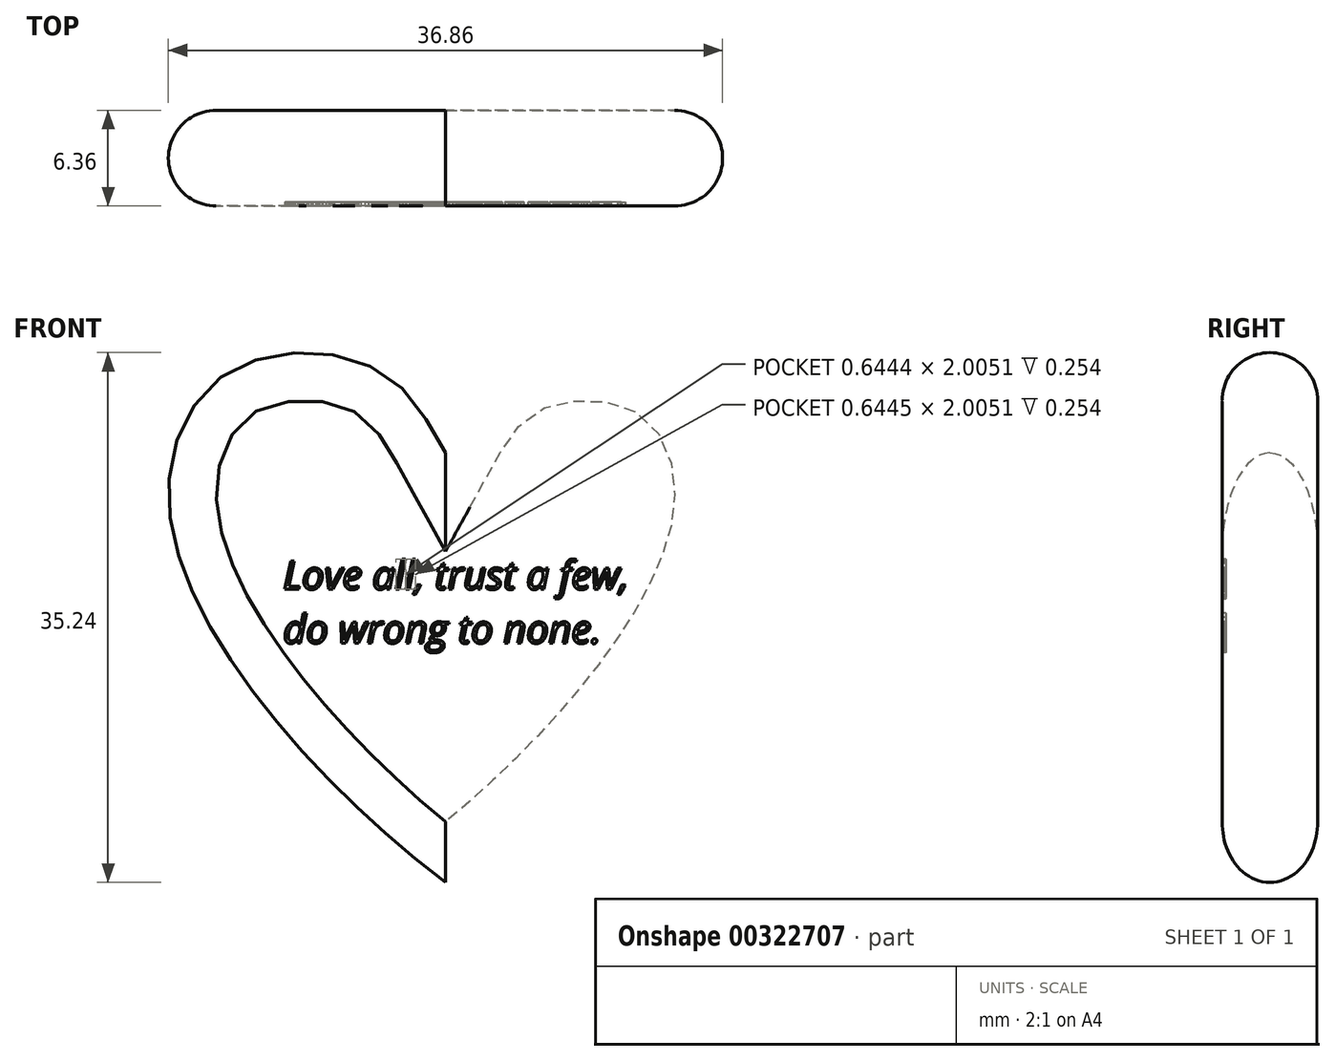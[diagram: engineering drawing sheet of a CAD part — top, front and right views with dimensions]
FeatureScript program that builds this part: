
annotation { "Feature Type Name" : "Feature", "Feature Type Description" : "" }
export const myFeature = defineFeature(function(context is Context, id is Id, definition is map)
    precondition{}
    {
        {
            var Q0;
            Q0=qCreatedBy(makeId("Front.planeOp"),FACE);
            var sketch = newSketch(context, id + "F0", { "sketchPlane" : qUnion([Q0])});
            skLineSegment(sketch, "E0", {"start": v(0, -28.57) * mm, "end": v(0, 0) * mm});
            skFitSpline(sketch, "E1", {"points": [v(0, 0) * mm, v(-4.62, 5.57) * mm, v(-14.08, 5.57) * mm, v(-18.41, -2.03) * mm, v(-14.08, -14.1) * mm, v(0, -28.58) * mm], "startDerivative": vector(-22.34, 40.38) * mm, "endDerivative": vector(58.02, -43.63) * mm});
            skFitSpline(sketch, "E2.MirrorCS", {"points": [v(0, 0) * mm, v(4.62, 5.57) * mm, v(14.08, 5.57) * mm, v(18.41, -2.03) * mm, v(14.08, -14.1) * mm, v(0, -28.58) * mm], "startDerivative": vector(22.34, 40.38) * mm, "endDerivative": vector(-58.02, -43.63) * mm});
            skSolve(sketch);
        }
        {
            var Q0;
            Q0=makeQuery(id+"F0.imprint","IMPRINT",FACE,{"disambiguationData":[TD([[makeQuery(id+"F0.imprint","IMPRINT",EDGE,{"derivedFrom":sQuery(id+"F0.wireOp",EDGE,"E0")}),1.0]])]});
            var Q1;
            Q1=makeQuery(id+"F0.imprint","IMPRINT",FACE,{"disambiguationData":[TD([[makeQuery(id+"F0.imprint","IMPRINT",EDGE,{"derivedFrom":sQuery(id+"F0.wireOp",EDGE,"E0")}),-1.0]])]});
            extrude(context, id + "F1", {"entities" : qUnion([Q0, Q1]), "endBound" : BoundingType.SYMMETRIC, "depth" : 6.35 * mm});
        }
        {
            var Q0;
            Q0=makeQuery(id+"F1.opExtrude","CAP_FACE",FACE,{"disambiguationData":[OSD([sQuery(id+"F0.wireOp",EDGE,"E1"),sQuery(id+"F0.wireOp",EDGE,"E2.MirrorCS")])],"isStart":false});
            var Q1;
            Q1=makeQuery(id+"F1.opExtrude","CAP_FACE",FACE,{"disambiguationData":[OSD([sQuery(id+"F0.wireOp",EDGE,"E1"),sQuery(id+"F0.wireOp",EDGE,"E2.MirrorCS")])],"isStart":true});
            fillet(context, id + "F2", {"entities" : qUnion([Q0, Q1]), "radius" : 3.17 * mm, "tangentPropagation" : true, "allowEdgeOverflow" : false});
        }
        {
            var Q0;
            Q0=makeQuery(id+"F1.opExtrude","CAP_FACE",FACE,{"disambiguationData":[OSD([sQuery(id+"F0.wireOp",EDGE,"E1"),sQuery(id+"F0.wireOp",EDGE,"E2.MirrorCS")])],"isStart":false});
            var sketch = newSketch(context, id + "F3", { "sketchPlane" : qUnion([Q0])});
            skText(sketch, "E3", { "text": "Love all, trust a few,\ndo wrong to none.", "fontName": "OpenSans-Italic.ttf"});
            const initialGuessF3  = {"E3": [-0.0108, -0.00908, 1, 0, 0.0019]};
            skSetInitialGuess(sketch, initialGuessF3);
            skSolve(sketch);
        }
        {
            var Q0;
            Q0 = qSketchRegion(id + "F3", true);
            extrude(context, id + "F4", {"entities" : qUnion([Q0]), "operationType" : NewBodyOperationType.REMOVE, "oppositeDirection" : true, "depth" : 0.25 * mm});
        }
    });
